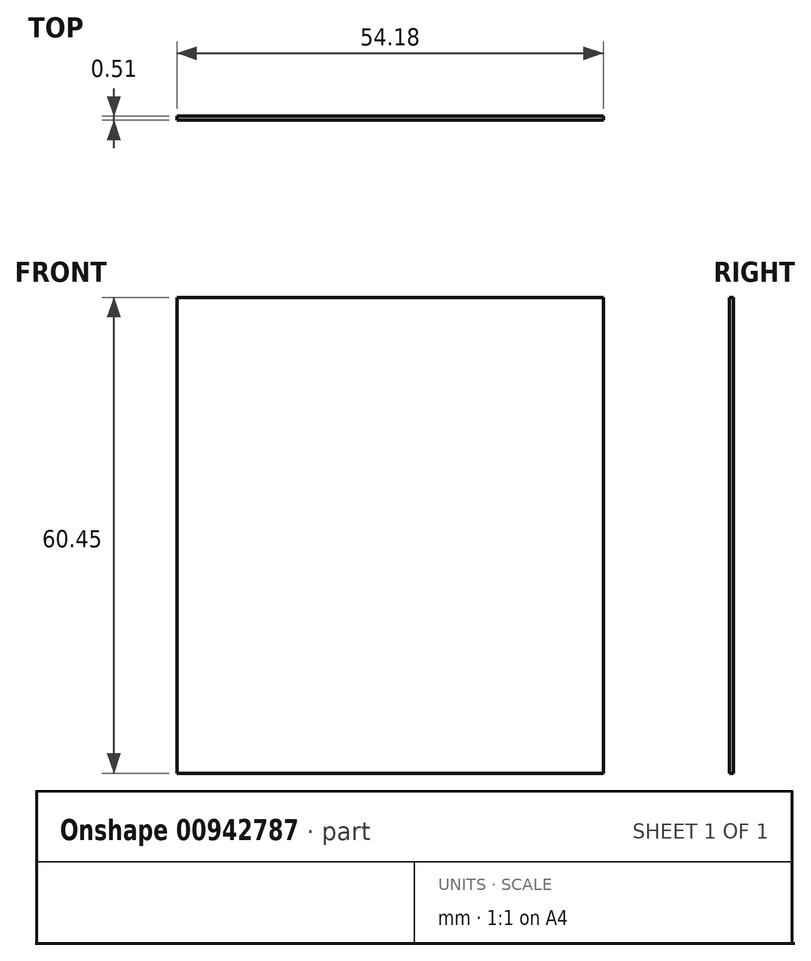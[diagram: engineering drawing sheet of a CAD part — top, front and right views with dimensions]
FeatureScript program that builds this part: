
annotation { "Feature Type Name" : "Feature", "Feature Type Description" : "" }
export const myFeature = defineFeature(function(context is Context, id is Id, definition is map)
    precondition{}
    {
        {
            var Q0;
            Q0=qCreatedBy(makeId("Front.planeOp"),FACE);
            var sketch = newSketch(context, id + "F0", { "sketchPlane" : qUnion([Q0])});
            skLineSegment(sketch, "E0.bottom", {"start": v(0, 0) * mm, "end": v(54.18, 0) * mm});
            skLineSegment(sketch, "E0.top", {"start": v(0, 60.45) * mm, "end": v(54.18, 60.45) * mm});
            skLineSegment(sketch, "E0.left", {"start": v(0, 0) * mm, "end": v(0, 60.45) * mm});
            skLineSegment(sketch, "E0.right", {"start": v(54.18, 0) * mm, "end": v(54.18, 60.45) * mm});
            skSolve(sketch);
        }
        {
            var Q0;
            Q0=makeQuery(id+"F0.imprint","IMPRINT",FACE,{"disambiguationData":[TD([[makeQuery(id+"F0.imprint","IMPRINT",EDGE,{"derivedFrom":sQuery(id+"F0.wireOp",EDGE,"E0.bottom")}),1.0]])]});
            extrude(context, id + "F1", {"entities" : qUnion([Q0]), "depth" : 0.5 * mm, "offsetDistance" : 25.4 * mm});
        }
    });
